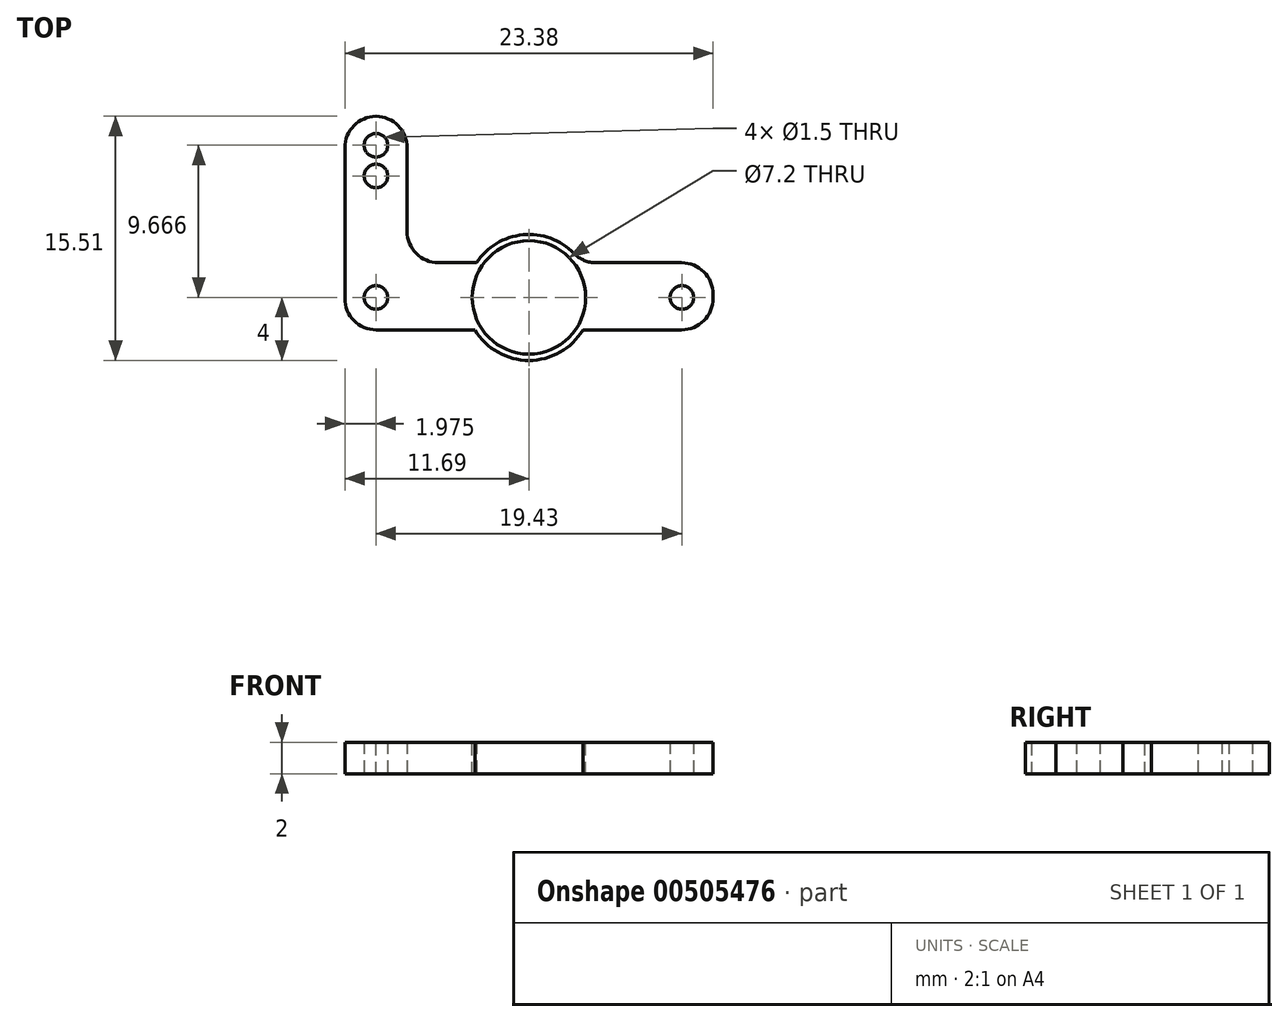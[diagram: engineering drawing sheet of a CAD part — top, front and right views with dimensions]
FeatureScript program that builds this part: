
annotation { "Feature Type Name" : "Feature", "Feature Type Description" : "" }
export const myFeature = defineFeature(function(context is Context, id is Id, definition is map)
    precondition{}
    {
        {
            var Q0;
            Q0=qCreatedBy(makeId("Top.planeOp"),FACE);
            var sketch = newSketch(context, id + "F0", { "sketchPlane" : qUnion([Q0])});
            skCircle(sketch, "E0", {"center": v(0, 0) * mm, "radius": 4 * mm});
            skLineSegment(sketch, "E1.bottom", {"start": v(3.34, 2.2) * mm, "end": v(11.7, 2.2) * mm});
            skLineSegment(sketch, "E1.top", {"start": v(3.34, -2.06) * mm, "end": v(11.7, -2.06) * mm});
            skLineSegment(sketch, "E1.left", {"start": v(3.34, 2.2) * mm, "end": v(3.34, -2.06) * mm});
            skLineSegment(sketch, "E1.right", {"start": v(11.7, 2.2) * mm, "end": v(11.7, -2.06) * mm});
            skLineSegment(sketch, "E2.bottom", {"start": v(11.7, 2.2) * mm, "end": v(7.74, 2.2) * mm});
            skLineSegment(sketch, "E2.top", {"start": v(11.7, 11.5) * mm, "end": v(7.74, 11.5) * mm});
            skLineSegment(sketch, "E2.left", {"start": v(11.7, 2.2) * mm, "end": v(11.7, 11.5) * mm});
            skLineSegment(sketch, "E2.right", {"start": v(7.74, 2.2) * mm, "end": v(7.74, 11.5) * mm});
            skCircle(sketch, "E3", {"center": v(9.72, 9.67) * mm, "radius": 0.75 * mm});
            skPoint(sketch, "E3.centerSnap0", {"position": v(9.72, 11.5) * mm});
            skCircle(sketch, "E4", {"center": v(9.72, 7.72) * mm, "radius": 0.75 * mm});
            skCircle(sketch, "E5", {"center": v(9.72, 0) * mm, "radius": 0.75 * mm});
            skLineSegment(sketch, "E6.MirrorCS", {"start": v(-7.74, 2.2) * mm, "end": v(-7.74, 11.5) * mm});
            skLineSegment(sketch, "E7.MirrorCS", {"start": v(-11.7, 11.5) * mm, "end": v(-7.74, 11.5) * mm});
            skLineSegment(sketch, "E8.MirrorCS", {"start": v(-11.7, 2.2) * mm, "end": v(-11.7, 11.5) * mm});
            skLineSegment(sketch, "E9.MirrorCS", {"start": v(-11.7, 2.2) * mm, "end": v(-7.74, 2.2) * mm});
            skLineSegment(sketch, "E10.MirrorCS", {"start": v(-3.34, 2.2) * mm, "end": v(-11.7, 2.2) * mm});
            skLineSegment(sketch, "E11.MirrorCS", {"start": v(-3.34, 2.2) * mm, "end": v(-3.34, -2.06) * mm});
            skLineSegment(sketch, "E12.MirrorCS", {"start": v(-3.34, -2.06) * mm, "end": v(-11.7, -2.06) * mm});
            skLineSegment(sketch, "E13.MirrorCS", {"start": v(-11.7, 2.2) * mm, "end": v(-11.7, -2.06) * mm});
            skCircle(sketch, "E14.MirrorC", {"center": v(-9.72, 7.72) * mm, "radius": 0.75 * mm});
            skCircle(sketch, "E15.MirrorC", {"center": v(-9.72, 9.67) * mm, "radius": 0.75 * mm});
            skCircle(sketch, "E16.MirrorC", {"center": v(-9.72, 0) * mm, "radius": 0.75 * mm});
            skPoint(sketch, "E17.trimOffspring.end.orphan", {"position": v(0, 7.14) * mm});
            skSolve(sketch);
        }
        {
            var Q0;
            {var subQ1=sQuery(id+"F0.wireOp",EDGE,"E6.MirrorCS");Q0=makeQuery(id+"F0.imprint","IMPRINT",FACE,{"disambiguationData":[TD([[makeQuery(id+"F0.imprint","IMPRINT",EDGE,{"derivedFrom":subQ1}),1.0]])]});}
            var Q1;
            {var subQ0=sQuery(id+"F0.wireOp",EDGE,"E13.MirrorCS");Q1=makeQuery(id+"F0.imprint","IMPRINT",FACE,{"disambiguationData":[TD([[makeQuery(id+"F0.imprint","IMPRINT",EDGE,{"derivedFrom":subQ0}),1.0]])]});}
            var Q2;
            {var subQ0=sQuery(id+"F0.wireOp",EDGE,"E1.left");Q2=makeQuery(id+"F0.imprint","IMPRINT",FACE,{"disambiguationData":[TD([[makeQuery(id+"F0.imprint","IMPRINT",EDGE,{"derivedFrom":subQ0}),-1.0]])]});}
            var Q3;
            {var subQ4=sQuery(id+"F0.wireOp",EDGE,"E1.bottom");Q3=makeQuery(id+"F0.imprint","IMPRINT",FACE,{"disambiguationData":[TD([[makeQuery(id+"F0.imprint","IMPRINT",EDGE,{"derivedFrom":subQ4}),-1.0]])]});}
            var Q4;
            Q4=makeQuery(id+"F0.imprint","IMPRINT",FACE,{"disambiguationData":[TD([[makeQuery(id+"F0.imprint","IMPRINT",EDGE,{"derivedFrom":sQuery(id+"F0.wireOp",EDGE,"E2.bottom")}),-1.0]])]});
            var Q5;
            {var subQ0=sQuery(id+"F0.wireOp",EDGE,"E11.MirrorCS");Q5=makeQuery(id+"F0.imprint","IMPRINT",FACE,{"disambiguationData":[TD([[makeQuery(id+"F0.imprint","IMPRINT",EDGE,{"derivedFrom":subQ0}),-1.0]])]});}
            var Q6;
            {var subQ0=sQuery(id+"F0.wireOp",EDGE,"E1.left");Q6=makeQuery(id+"F0.imprint","IMPRINT",FACE,{"disambiguationData":[TD([[makeQuery(id+"F0.imprint","IMPRINT",EDGE,{"derivedFrom":subQ0}),1.0]])]});}
            extrude(context, id + "F1", {"entities" : qUnion([Q0, Q1, Q2, Q3, Q4, Q5, Q6]), "depth" : 2 * mm});
        }
        {
            var Q0;
            Q0=makeQuery(id+"F1.opExtrude","CAP_FACE",FACE,{"disambiguationData":[OSD([sQuery(id+"F0.wireOp",EDGE,"E0"),sQuery(id+"F0.wireOp",EDGE,"E1.bottom"),sQuery(id+"F0.wireOp",EDGE,"E1.top"),sQuery(id+"F0.wireOp",EDGE,"E1.right"),sQuery(id+"F0.wireOp",EDGE,"E2.top"),sQuery(id+"F0.wireOp",EDGE,"E2.left"),sQuery(id+"F0.wireOp",EDGE,"E2.right"),sQuery(id+"F0.wireOp",EDGE,"E3"),sQuery(id+"F0.wireOp",EDGE,"E4"),sQuery(id+"F0.wireOp",EDGE,"E5"),sQuery(id+"F0.wireOp",EDGE,"E6.MirrorCS"),sQuery(id+"F0.wireOp",EDGE,"E7.MirrorCS"),sQuery(id+"F0.wireOp",EDGE,"E8.MirrorCS"),sQuery(id+"F0.wireOp",EDGE,"E10.MirrorCS"),sQuery(id+"F0.wireOp",EDGE,"E12.MirrorCS"),sQuery(id+"F0.wireOp",EDGE,"E13.MirrorCS"),sQuery(id+"F0.wireOp",EDGE,"E14.MirrorC"),sQuery(id+"F0.wireOp",EDGE,"E15.MirrorC"),sQuery(id+"F0.wireOp",EDGE,"E16.MirrorC")])],"isStart":false});
            var sketch = newSketch(context, id + "F2", { "sketchPlane" : qUnion([Q0])});
            skCircle(sketch, "E18", {"center": v(0, 0) * mm, "radius": 3.6 * mm});
            skSolve(sketch);
        }
        {
            var Q0;
            Q0=makeQuery(id+"F2.imprint","IMPRINT",FACE,{"disambiguationData":[TD([[makeQuery(id+"F2.imprint","IMPRINT",EDGE,{"derivedFrom":sQuery(id+"F2.wireOp",EDGE,"E18")}),1.0]])]});
            extrude(context, id + "F3", {"entities" : qUnion([Q0]), "operationType" : NewBodyOperationType.REMOVE, "oppositeDirection" : true, "depth" : 25 * mm});
        }
        {
            var Q0;
            Q0=makeQuery(id+"F1.opExtrude","SWEPT_EDGE",EDGE,{"disambiguationData":[OSD([sQuery(id+"F0.wireOp",EDGE,"E2.top"),sQuery(id+"F0.wireOp",EDGE,"E2.left")])]});
            var Q1;
            Q1=makeQuery(id+"F1.opExtrude","SWEPT_EDGE",EDGE,{"disambiguationData":[OSD([sQuery(id+"F0.wireOp",EDGE,"E2.top"),sQuery(id+"F0.wireOp",EDGE,"E2.right")])]});
            var Q2;
            Q2=makeQuery(id+"F1.opExtrude","SWEPT_EDGE",EDGE,{"disambiguationData":[OSD([sQuery(id+"F0.wireOp",EDGE,"E6.MirrorCS"),sQuery(id+"F0.wireOp",EDGE,"E7.MirrorCS")])]});
            var Q3;
            Q3=makeQuery(id+"F1.opExtrude","SWEPT_EDGE",EDGE,{"disambiguationData":[OSD([sQuery(id+"F0.wireOp",EDGE,"E7.MirrorCS"),sQuery(id+"F0.wireOp",EDGE,"E8.MirrorCS")])]});
            var Q4;
            Q4=makeQuery(id+"F1.opExtrude","SWEPT_EDGE",EDGE,{"disambiguationData":[OSD([sQuery(id+"F0.wireOp",EDGE,"E12.MirrorCS"),sQuery(id+"F0.wireOp",EDGE,"E13.MirrorCS")])]});
            var Q5;
            Q5=makeQuery(id+"F1.opExtrude","SWEPT_EDGE",EDGE,{"disambiguationData":[OSD([sQuery(id+"F0.wireOp",EDGE,"E1.top"),sQuery(id+"F0.wireOp",EDGE,"E1.right")])]});
            var Q6;
            Q6=makeQuery(id+"F1.opExtrude","SWEPT_EDGE",EDGE,{"disambiguationData":[OSD([sQuery(id+"F0.wireOp",EDGE,"E6.MirrorCS"),sQuery(id+"F0.wireOp",EDGE,"E10.MirrorCS")])]});
            var Q7;
            Q7=makeQuery(id+"F1.opExtrude","SWEPT_EDGE",EDGE,{"disambiguationData":[OSD([sQuery(id+"F0.wireOp",EDGE,"E1.bottom"),sQuery(id+"F0.wireOp",EDGE,"E2.bottom"),sQuery(id+"F0.wireOp",EDGE,"E2.right")])]});
            fillet(context, id + "F4", {"entities" : qUnion([Q0, Q1, Q2, Q3, Q4, Q5, Q6, Q7]), "radius" : 2 * mm, "tangentPropagation" : true, "allowEdgeOverflow" : false});
        }
    });
